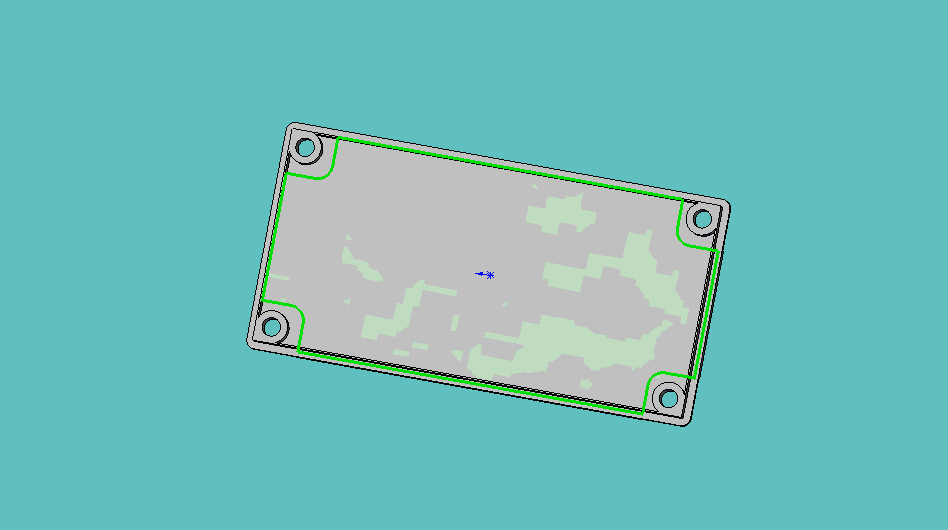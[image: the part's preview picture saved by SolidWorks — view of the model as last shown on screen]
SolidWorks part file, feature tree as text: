
SOLIDWORKS PART (.sldprt)
format: sldprt  version: not decoded by parser v0  size: 245,760 bytes
history: native  units: mm
features: sketch x3, extrude x2, mirror x2, material x1, fillet x1, cut_extrude x1 (+13 scaffold rows collapsed)
feature tree (23):
  scaffold x13  (default folders/planes/origin — collapsed)
  material  "ABS"
  sketch  "Sketch1"  dims[D1=~2.38125mm]
  extrude  "Extrude1"  Depth=1.5875mm
  fillet  "Fillet2"  Radius=0.508mm
  sketch  "Sketch2"  dims[D1=0.635mm]
  extrude  "Extrude2"  Depth=1.27mm
  sketch  "Sketch3"  dims[c1.D1=~1.841454mm c2.D1=45.0deg c2.D2=4.318mm]
  cut_extrude  "Cut-Extrude1"  Depth=0.508mm
  mirror  "Mirror1"
  mirror  "Mirror2"
decode coverage: 7 of 9 modeling features carry decoded parameters
note: ~ marks probable driven/reference dimensions
note: suppression state not decoded; provenance and decode notes live in map.json
